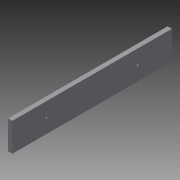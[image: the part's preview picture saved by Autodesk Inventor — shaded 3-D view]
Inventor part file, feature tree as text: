
AUTODESK INVENTOR PART (.ipt)
format: ipt  version: 2015 SP1 (Build 190203100, 203)  size: 83,968 bytes
history: native  units: in
note: dims shown in document units (in); Inventor stores cm internally (conversion verified against a paired STEP export)
features: sketch x2, extrude x1, hole x1, projected_geometry x1
ambient origin geometry x8: Origin, YZ Plane, XZ Plane, XY Plane, X Axis, Y Axis, Z Axis, Center Point
bodies: Solid1 (feature_tree)
feature tree (5):
  extrude  "Extrusion1"  Depth=5.0in
  hole  "Hole1"  [1 undecoded]
  sketch  "Sketch1"  dims[d0=0.75in d1=5.0in]
  sketch  "Sketch4"  dims[d2=28.0in d3=0.0in d18=2.5in d19=2.5in d20=6.5in d21=6.5in d22=0.3125in d23=0.75in d24=0.375in d25=0.25in d26=0.5635in d27=1.0in d28=0.8108in]
  projected_geometry  "Projected Loop3"
note: 1 required parameter value undecoded (feature->parameter linkage not recoverable at this tier; creation-order binding heuristic only, values carry confidence <= 0.55)
